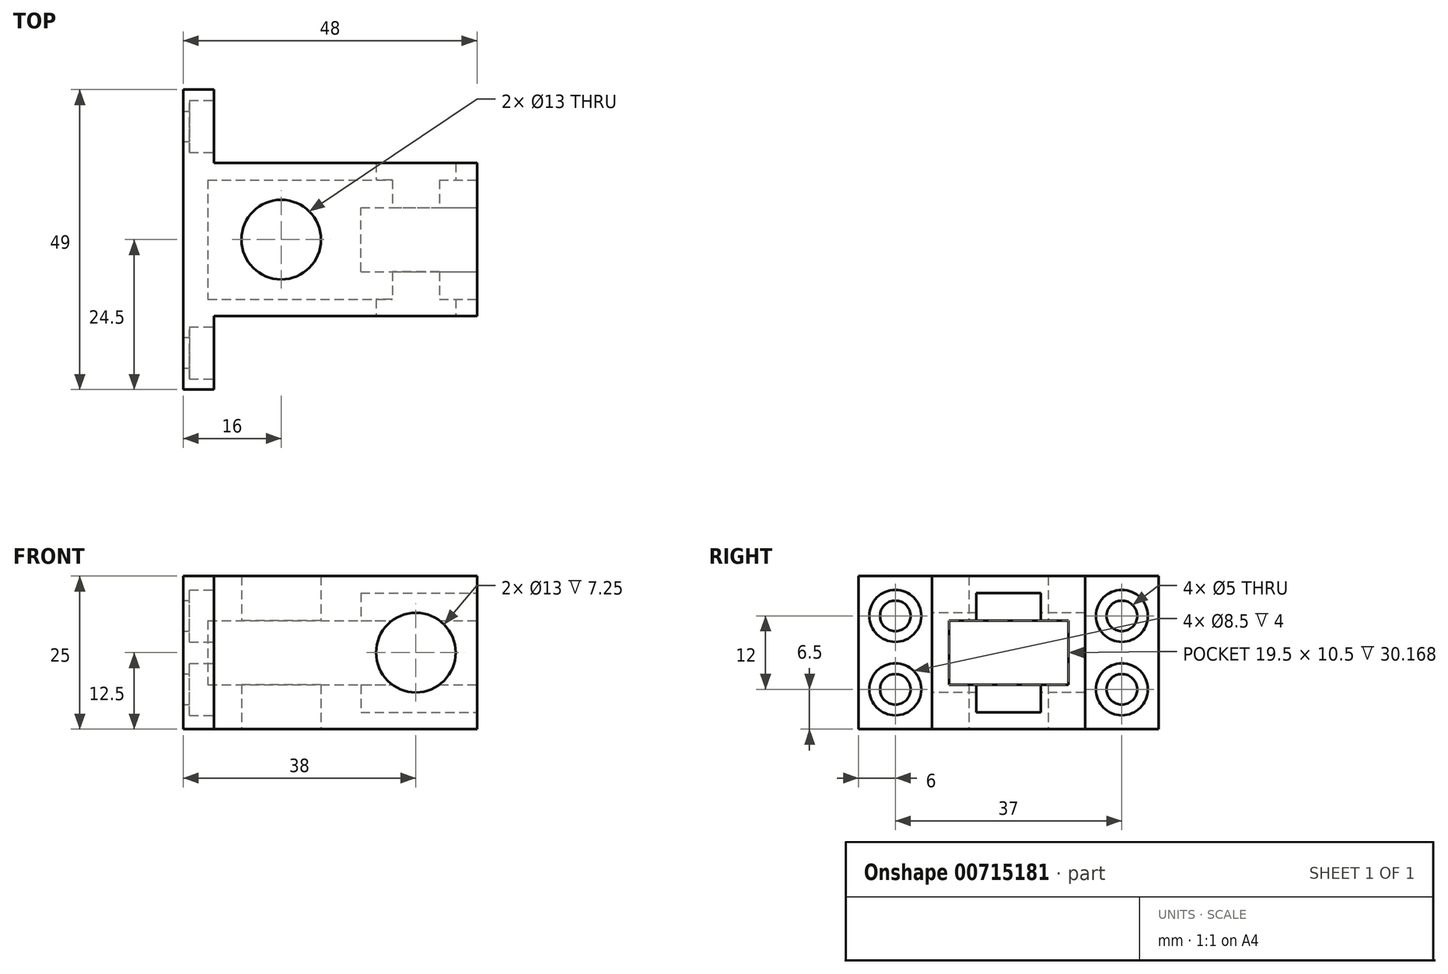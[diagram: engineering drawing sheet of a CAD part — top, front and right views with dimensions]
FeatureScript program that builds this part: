
annotation { "Feature Type Name" : "Feature", "Feature Type Description" : "" }
export const myFeature = defineFeature(function(context is Context, id is Id, definition is map)
    precondition{}
    {
        {
            var Q0;
            Q0=qCreatedBy(makeId("Top.planeOp"),FACE);
            var sketch = newSketch(context, id + "F0", { "sketchPlane" : qUnion([Q0])});
            skLineSegment(sketch, "E0.bottom", {"start": v(-16, -12.5) * mm, "end": v(32, -12.5) * mm});
            skLineSegment(sketch, "E0.top", {"start": v(-16, 12.5) * mm, "end": v(32, 12.5) * mm});
            skLineSegment(sketch, "E0.left", {"start": v(-16, -12.5) * mm, "end": v(-16, 12.5) * mm});
            skLineSegment(sketch, "E0.right", {"start": v(32, -12.5) * mm, "end": v(32, 12.5) * mm});
            skLineSegment(sketch, "E1", {"start": v(0, 0) * mm, "end": v(-20.8, 0) * mm, "construction": true});
            skSolve(sketch);
        }
        {
            var Q0;
            Q0 = qSketchRegion(id + "F0", true);
            extrude(context, id + "F1", {"entities" : qUnion([Q0]), "endBound" : BoundingType.SYMMETRIC, "depth" : 25 * mm, "offsetDistance" : 25 * mm});
        }
        {
            var Q0;
            Q0=makeQuery(id+"F1.opExtrude","SWEPT_FACE",FACE,{"disambiguationData":[OSD([sQuery(id+"F0.wireOp",EDGE,"E0.right")])]});
            var sketch = newSketch(context, id + "F2", { "sketchPlane" : qUnion([Q0])});
            skLineSegment(sketch, "E2.bottom", {"start": v(9.75, 5.25) * mm, "end": v(-9.75, 5.25) * mm});
            skLineSegment(sketch, "E2.top", {"start": v(9.75, -5.25) * mm, "end": v(-9.75, -5.25) * mm});
            skLineSegment(sketch, "E2.left", {"start": v(9.75, 5.25) * mm, "end": v(9.75, -5.25) * mm});
            skLineSegment(sketch, "E2.right", {"start": v(-9.75, 5.25) * mm, "end": v(-9.75, -5.25) * mm});
            skPoint(sketch, "E2.middle", {"position": v(0, 0) * mm});
            skSolve(sketch);
        }
        {
            var Q0;
            Q0 = qSketchRegion(id + "F2", true);
            extrude(context, id + "F3", {"entities" : qUnion([Q0]), "operationType" : NewBodyOperationType.REMOVE, "oppositeDirection" : true, "depth" : 44 * mm, "offsetDistance" : 25 * mm});
        }
        {
            var Q0;
            Q0=makeQuery(id+"F1.opExtrude","CAP_FACE",FACE,{"disambiguationData":[OSD([sQuery(id+"F0.wireOp",EDGE,"E0.bottom"),sQuery(id+"F0.wireOp",EDGE,"E0.top"),sQuery(id+"F0.wireOp",EDGE,"E0.left"),sQuery(id+"F0.wireOp",EDGE,"E0.right")])],"isStart":true});
            var sketch = newSketch(context, id + "F4", { "sketchPlane" : qUnion([Q0])});
            skCircle(sketch, "E3", {"center": v(0, 0) * mm, "radius": 6.5 * mm});
            skSolve(sketch);
        }
        {
            var Q0;
            Q0 = qSketchRegion(id + "F4", true);
            extrude(context, id + "F5", {"entities" : qUnion([Q0]), "operationType" : NewBodyOperationType.REMOVE, "endBound" : BoundingType.THROUGH_ALL, "oppositeDirection" : true, "depth" : 25 * mm, "offsetDistance" : 25 * mm});
        }
        {
            var Q0;
            Q0=makeQuery(id+"F1.opExtrude","SWEPT_FACE",FACE,{"disambiguationData":[OSD([sQuery(id+"F0.wireOp",EDGE,"E0.right")])]});
            var sketch = newSketch(context, id + "F6", { "sketchPlane" : qUnion([Q0])});
            skLineSegment(sketch, "E4.bottom", {"start": v(5.25, 9.75) * mm, "end": v(-5.25, 9.75) * mm});
            skLineSegment(sketch, "E4.top", {"start": v(5.25, -9.75) * mm, "end": v(-5.25, -9.75) * mm});
            skLineSegment(sketch, "E4.left", {"start": v(5.25, 9.75) * mm, "end": v(5.25, -9.75) * mm});
            skLineSegment(sketch, "E4.right", {"start": v(-5.25, 9.75) * mm, "end": v(-5.25, -9.75) * mm});
            skPoint(sketch, "E4.middle", {"position": v(0, 0) * mm});
            skSolve(sketch);
        }
        {
            var Q0;
            Q0 = qSketchRegion(id + "F6", true);
            extrude(context, id + "F7", {"entities" : qUnion([Q0]), "operationType" : NewBodyOperationType.REMOVE, "oppositeDirection" : true, "depth" : 19 * mm, "offsetDistance" : 25 * mm});
        }
        {
            var Q0;
            Q0=makeQuery(id+"F1.opExtrude","SWEPT_FACE",FACE,{"disambiguationData":[OSD([sQuery(id+"F0.wireOp",EDGE,"E0.bottom")])]});
            var sketch = newSketch(context, id + "F8", { "sketchPlane" : qUnion([Q0])});
            skCircle(sketch, "E5", {"center": v(22, 0) * mm, "radius": 6.5 * mm});
            skSolve(sketch);
        }
        {
            var Q0;
            Q0 = qSketchRegion(id + "F8", true);
            extrude(context, id + "F9", {"entities" : qUnion([Q0]), "operationType" : NewBodyOperationType.REMOVE, "endBound" : BoundingType.THROUGH_ALL, "oppositeDirection" : true, "depth" : 25 * mm, "offsetDistance" : 25 * mm});
        }
        {
            var Q0;
            Q0=makeQuery(id+"F1.opExtrude","SWEPT_FACE",FACE,{"disambiguationData":[OSD([sQuery(id+"F0.wireOp",EDGE,"E0.left")])]});
            var sketch = newSketch(context, id + "F10", { "sketchPlane" : qUnion([Q0])});
            skLineSegment(sketch, "E6.bottom", {"start": v(-12.5, 12.5) * mm, "end": v(-24.5, 12.5) * mm});
            skLineSegment(sketch, "E6.top", {"start": v(-12.5, -12.5) * mm, "end": v(-24.5, -12.5) * mm});
            skLineSegment(sketch, "E6.left", {"start": v(-12.5, 12.5) * mm, "end": v(-12.5, -12.5) * mm});
            skLineSegment(sketch, "E6.right", {"start": v(-24.5, 12.5) * mm, "end": v(-24.5, -12.5) * mm});
            skLineSegment(sketch, "E7.bottom", {"start": v(12.5, 12.5) * mm, "end": v(24.5, 12.5) * mm});
            skLineSegment(sketch, "E7.top", {"start": v(12.5, -12.5) * mm, "end": v(24.5, -12.5) * mm});
            skLineSegment(sketch, "E7.left", {"start": v(12.5, 12.5) * mm, "end": v(12.5, -12.5) * mm});
            skLineSegment(sketch, "E7.right", {"start": v(24.5, 12.5) * mm, "end": v(24.5, -12.5) * mm});
            skSolve(sketch);
        }
        {
            var Q0;
            Q0 = qSketchRegion(id + "F10", true);
            extrude(context, id + "F11", {"entities" : qUnion([Q0]), "operationType" : NewBodyOperationType.ADD, "oppositeDirection" : true, "depth" : 5 * mm, "offsetDistance" : 25 * mm});
        }
        {
            var Q0;
            Q0=makeQuery(id+"F11.opExtrude","CAP_FACE",FACE,{"disambiguationData":[OSD([sQuery(id+"F10.wireOp",EDGE,"E7.bottom"),sQuery(id+"F10.wireOp",EDGE,"E7.top"),sQuery(id+"F10.wireOp",EDGE,"E7.left"),sQuery(id+"F10.wireOp",EDGE,"E7.right")])],"isStart":false});
            var sketch = newSketch(context, id + "F12", { "sketchPlane" : qUnion([Q0])});
            skPoint(sketch, "E8", {"position": v(-18.5, 6) * mm});
            skPoint(sketch, "E9", {"position": v(-18.5, -6) * mm});
            skPoint(sketch, "E10", {"position": v(18.5, 6) * mm});
            skPoint(sketch, "E11", {"position": v(18.5, -6) * mm});
            skSolve(sketch);
        }
        {
            var Q0;
            Q0=sQuery(id+"F12.wireOp",VERTEX,"E8");
            var Q1;
            Q1=sQuery(id+"F12.wireOp",VERTEX,"E9");
            var Q2;
            Q2=sQuery(id+"F12.wireOp",VERTEX,"E10");
            var Q3;
            Q3=sQuery(id+"F12.wireOp",VERTEX,"E11");
            var Q4;
            Q4=makeQuery(id+"F1.opExtrude","SWEPT_BODY",BODY,{"disambiguationData":[OSD([sQuery(id+"F0.wireOp",EDGE,"E0.bottom"),sQuery(id+"F0.wireOp",EDGE,"E0.top"),sQuery(id+"F0.wireOp",EDGE,"E0.left"),sQuery(id+"F0.wireOp",EDGE,"E0.right")])]});
            hole(context, id + "F13", {"style" : HoleStyle.C_BORE, "endStyle" : HoleEndStyle.THROUGH, "holeDiameter" : 5 * mm, "cBoreDiameter" : 8.5 * mm, "cBoreDepth" : 4 * mm, "majorDiameter" : 5 * mm, "isTappedThrough" : true, "tappedDepth" : 12 * mm, "tapClearance" : 3, "locations" : qUnion([Q0, Q1, Q2, Q3]), "scope" : qUnion([Q4])});
        }
    });
